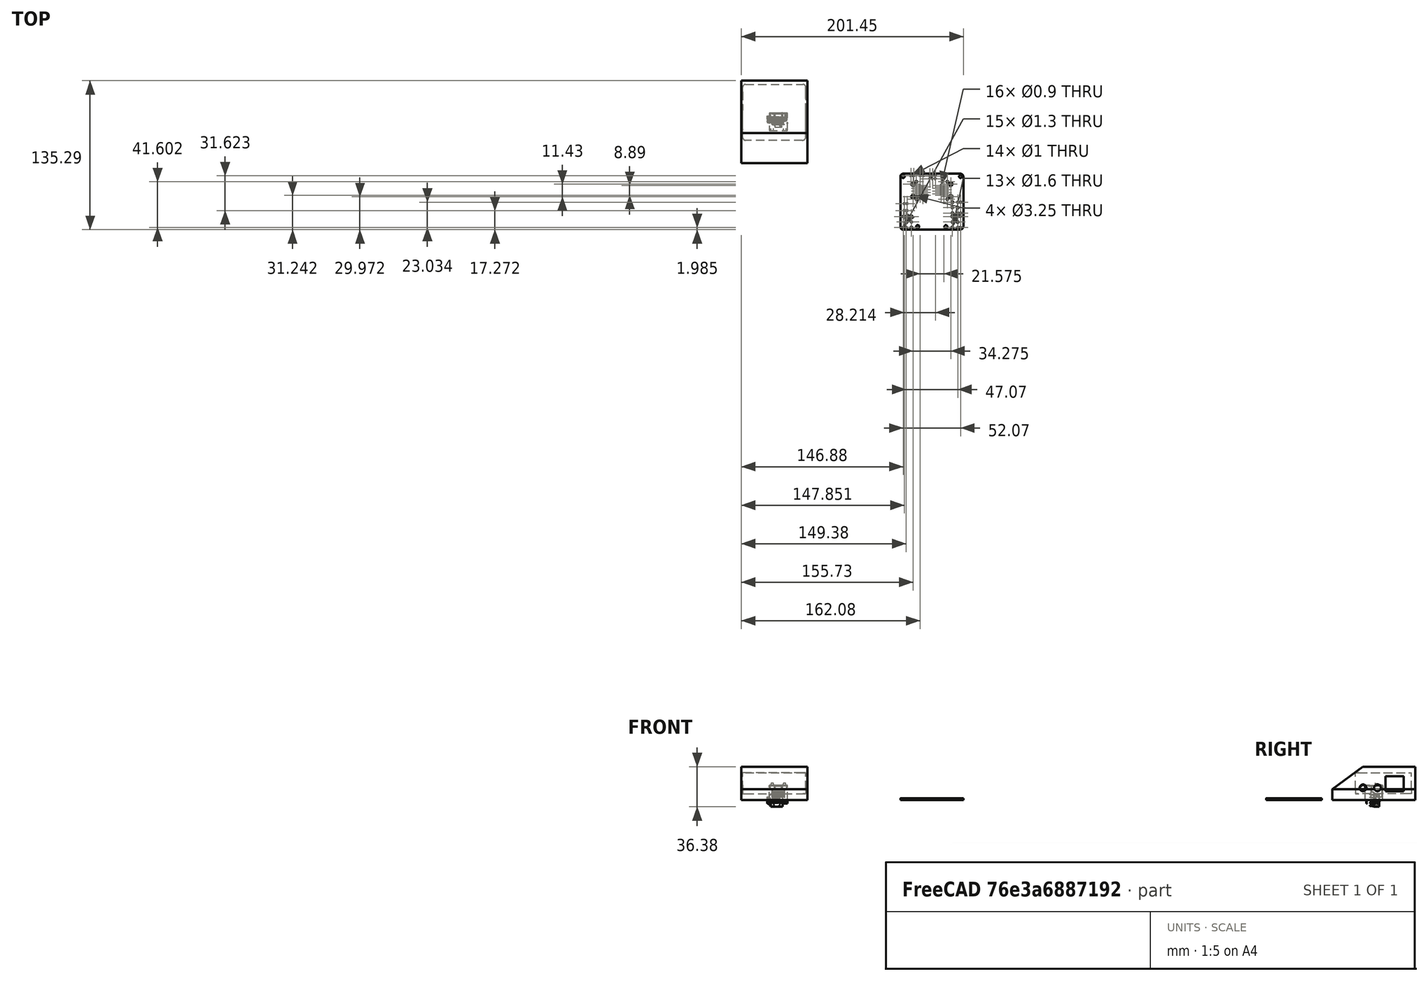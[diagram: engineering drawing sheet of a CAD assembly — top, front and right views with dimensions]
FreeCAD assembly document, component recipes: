
FREECAD ASSEMBLY — COMPONENT RECIPES ("Mikadapter81X")

This assembly document has 4 components, labeled P0..P3 below (a component is one placed body or linked part). 2 of them carry a construction recipe — the FreeCAD feature program that regenerates the part from scratch, quoted from this document or its linked companion documents; the rest are supplied as boundary geometry only. No exploded tour is included for this assembly.
COMPONENT P0 — recipe-attached ("Body", modeled in this document).
Construction recipe (the document's own serialized feature program — sketch geometry with constraints, then the solid features built on it; lengths are millimeters unless a unit is written):

FEATURE [PartDesign::SubShapeBinder] Binder
  BindMode = 0
  ClaimChildren = false
  Context = -> Body [Binder.]
  Fuse = false
  MakeFace = true
  PartialLoad = false
  Relative = true
  Support = -> [LinkGroup]
  _Version = 2
FEATURE [Sketcher::SketchObject] Sketch
  ExternalGeometry = -> [Binder]
  FullyConstrained = true
  MapMode = 5
  Support = -> [XY_Plane]
  sketch-geometry (4):
    g0: LineSegment StartX=-30 StartY=37.5 StartZ=0 EndX=30 EndY=37.5 EndZ=0
    g1: LineSegment StartX=30 StartY=37.5 StartZ=0 EndX=30 EndY=-37.5 EndZ=0
    g2: LineSegment StartX=30 StartY=-37.5 StartZ=0 EndX=-30 EndY=-37.5 EndZ=0
    g3: LineSegment StartX=-30 StartY=-37.5 StartZ=0 EndX=-30 EndY=37.5 EndZ=0
  constraints (11):
    c: Coincident(g0,g1)
    c: Coincident(g1,g2)
    c: Coincident(g2,g3)
    c: Coincident(g3,g0)
    c: Horizontal(g0)
    c: Horizontal(g2)
    c: Vertical(g1)
    c: Vertical(g3)
    c: Symmetric(g1,g0,g-1)
    c: Distance(g0) = 60
    c: Distance(g3) = 75
FEATURE [PartDesign::Pad] Pad
  Direction = (1,1,1)
  Length = 10
  Length2 = 100
  Profile = -> Sketch
  Type = 0
FEATURE [Sketcher::SketchObject] Sketch001
  ExternalGeometry = -> [Binder]
  FullyConstrained = true
  MapMode = 5
  Placement = pos=(0,0,10) rot=(0,0,1;0rad)
  Support = -> [Pad]
  sketch-geometry (8):
    g0: LineSegment StartX=-26.16 StartY=34.1318 StartZ=0 EndX=25.91 EndY=34.1318 EndZ=0
    g1: LineSegment StartX=-28.7 StartY=31.5918 StartZ=0 EndX=-28.7 EndY=-14.1282 EndZ=0
    g2: LineSegment StartX=-26.16 StartY=-16.6682 StartZ=0 EndX=25.275 EndY=-16.6682 EndZ=0
    g3: LineSegment StartX=28.45 StartY=31.5918 StartZ=0 EndX=28.45 EndY=-13.4932 EndZ=0
    g4: ArcOfCircle CenterX=-26.16 CenterY=31.5918 CenterZ=0 NormalX=0 NormalY=0 NormalZ=1 AngleXU=0 Radius=2.53997 StartAngle=1.57078 EndAngle=3.1416
    g5: ArcOfCircle CenterX=25.91 CenterY=31.5918 CenterZ=0 NormalX=0 NormalY=0 NormalZ=1 AngleXU=0 Radius=2.53999 StartAngle=6.28318 EndAngle=7.85399
    g6: ArcOfCircle CenterX=25.275 CenterY=-13.4932 CenterZ=0 NormalX=0 NormalY=0 NormalZ=1 AngleXU=0 Radius=3.17501 StartAngle=4.71239 EndAngle=6.28318
    g7: ArcOfCircle CenterX=-26.16 CenterY=-14.1282 CenterZ=0 NormalX=0 NormalY=0 NormalZ=1 AngleXU=0 Radius=2.53999 StartAngle=3.14159 EndAngle=4.71239
  constraints (20):
    c: Coincident(g0,g-3)
    c: Coincident(g0,g-3)
    c: Coincident(g1,g-5)
    c: Coincident(g-5,g1)
    c: Coincident(g2,g-7)
    c: Coincident(g2,g-7)
    c: Coincident(g3,g-9)
    c: Coincident(g3,g-9)
    c: Coincident(g4,g-4)
    c: Coincident(g4,g1)
    c: Coincident(g4,g0)
    c: Coincident(g5,g-10)
    c: Coincident(g5,g0)
    c: Coincident(g5,g3)
    c: Coincident(g6,g-8)
    c: Coincident(g6,g2)
    c: Coincident(g6,g3)
    c: Coincident(g7,g-6)
    c: Coincident(g7,g1)
    c: Coincident(g7,g2)
FEATURE [PartDesign::Pocket] Pocket
  BaseFeature = -> Pad
  Length = 4
  Length2 = 100
  Profile = -> Sketch001
  Type = 0
FEATURE [Sketcher::SketchObject] Sketch002
  ExternalGeometry = -> [Binder,Pocket]
  FullyConstrained = false
  MapMode = 5
  Placement = pos=(30,0,0) rot=(0.57735,0.57735,0.57735;2.0944rad)
  Support = -> [Pocket]
  sketch-geometry (6):
    g0: LineSegment StartX=10.6588 StartY=21.6555 StartZ=0 EndX=27.1688 EndY=21.6555 EndZ=0
    g1: LineSegment StartX=27.1688 StartY=21.6555 StartZ=0 EndX=27.1688 EndY=8.19554 EndZ=0
    g2: LineSegment StartX=27.1688 StartY=8.19554 StartZ=0 EndX=10.6588 EndY=8.19554 EndZ=0
    g3: LineSegment StartX=10.6588 StartY=8.19554 StartZ=0 EndX=10.6588 EndY=21.6555 EndZ=0
    g4: Circle CenterX=3.3622 CenterY=11.2293 CenterZ=0 NormalX=0 NormalY=0 NormalZ=1 AngleXU=0 Radius=3.00378
    g5: Circle CenterX=-9.8878 CenterY=11.2293 CenterZ=0 NormalX=0 NormalY=0 NormalZ=1 AngleXU=0 Radius=3.00378
  constraints (13):
    c: Coincident(g0,g1)
    c: Coincident(g1,g2)
    c: Coincident(g2,g3)
    c: Coincident(g3,g0)
    c: Horizontal(g0)
    c: Horizontal(g2)
    c: Vertical(g1)
    c: Vertical(g3)
    c: Coincident(g0,g-9)
    c: Coincident(g1,g-11)
    c: DistanceY(g4,g5) = 0
    c: DistanceX(g5,g4) = 13.25
    c: Equal(g4,g5)
FEATURE [PartDesign::Pocket] Pocket001
  BaseFeature = -> Pocket
  Length = 5
  Length2 = 100
  Profile = -> Sketch002
  Type = 0
FEATURE [PartDesign::SubShapeBinder] Binder001
  BindMode = 0
  ClaimChildren = false
  Context = -> Body [Binder001.]
  Fuse = false
  MakeFace = true
  PartialLoad = false
  Relative = true
  Support = -> [Binder]
  _Version = 2
FEATURE [PartDesign::Body] Body
  Group = -> [Sketch,Pad,Binder,Sketch001,Pocket,Sketch002,Pocket001,Binder001]
  Origin = -> Origin
  Tip = -> Pocket001
COMPONENT P1 — recipe-attached ("Body001", modeled in this document).
Construction recipe (the document's own serialized feature program — sketch geometry with constraints, then the solid features built on it; lengths are millimeters unless a unit is written):

FEATURE [PartDesign::SubShapeBinder] Binder003
  BindMode = 0
  ClaimChildren = false
  Fuse = false
  MakeFace = true
  PartialLoad = false
  Relative = true
  Support = -> [Body[Pocket001.]]
  _Version = 2
FEATURE [Sketcher::SketchObject] Sketch008
  ExternalGeometry = -> [Binder003]
  FullyConstrained = false
  MapMode = 5
  Placement = pos=(0,0,0) rot=(0.57735,0.57735,0.57735;2.0944rad)
  Support = -> [YZ_Plane001]
  sketch-geometry (4):
    g0: LineSegment StartX=-37.5 StartY=10 StartZ=0 EndX=37.5 EndY=10 EndZ=0
    g1: LineSegment StartX=37.5 StartY=10 StartZ=0 EndX=37.5 EndY=30.3769 EndZ=0
    g2: LineSegment StartX=-37.5 StartY=10 StartZ=0 EndX=-10.046 EndY=30.3769 EndZ=0
    g3: LineSegment StartX=-10.046 StartY=30.3769 StartZ=0 EndX=37.5 EndY=30.3769 EndZ=0
  constraints (7):
    c: Coincident(g0,g-3)
    c: Vertical(g1)
    c: Coincident(g2,g0)
    c: Coincident(g3,g2)
    c: Coincident(g3,g1)
    c: Horizontal(g3)
    c: Coincident(g1,g0)
FEATURE [PartDesign::Pad] Pad001
  Direction = (1,1,1)
  Length = 60
  Length2 = 100
  Midplane = true
  Placement = pos=(0,0,0) rot=(0.57735,0.57735,0.57735;2.0944rad)
  Profile = -> Sketch008
  Type = 0
FEATURE [PartDesign::SubShapeBinder] Binder004
  BindMode = 0
  ClaimChildren = false
  Context = -> Body001 [Binder004.]
  Fuse = false
  MakeFace = true
  PartialLoad = false
  Relative = true
  Support = -> [LinkGroup]
  _Version = 2
FEATURE [Sketcher::SketchObject] Sketch009
  ExternalGeometry = -> [Binder004]
  FullyConstrained = false
  MapMode = 5
  Placement = pos=(-2.8e-15,1.6e-15,10) rot=(0.707107,0.707107,0;3.14159rad)
  Support = -> [Pad001]
  sketch-geometry (8):
    g0: LineSegment StartX=-16.6682 StartY=25.275 StartZ=0 EndX=-16.6682 EndY=-26.16 EndZ=0
    g1: LineSegment StartX=-14.1282 StartY=-28.7 StartZ=0 EndX=31.5918 EndY=-28.7 EndZ=0
    g2: LineSegment StartX=34.1318 StartY=-26.16 StartZ=0 EndX=34.1318 EndY=25.91 EndZ=0
    g3: ArcOfCircle CenterX=-13.4932 CenterY=25.275 CenterZ=0 NormalX=0 NormalY=0 NormalZ=1 AngleXU=0 Radius=3.17501 StartAngle=1.5708 EndAngle=3.14159
    g4: ArcOfCircle CenterX=31.5918 CenterY=25.91 CenterZ=0 NormalX=0 NormalY=0 NormalZ=1 AngleXU=0 Radius=2.53999 StartAngle=6.28318 EndAngle=7.85399
    g5: ArcOfCircle CenterX=-14.1282 CenterY=-26.16 CenterZ=0 NormalX=0 NormalY=0 NormalZ=1 AngleXU=0 Radius=2.53999 StartAngle=3.14159 EndAngle=4.71239
    g6: ArcOfCircle CenterX=31.5918 CenterY=-26.16 CenterZ=0 NormalX=0 NormalY=0 NormalZ=1 AngleXU=0 Radius=2.53997 StartAngle=4.71238 EndAngle=6.28319
    g7: LineSegment StartX=-13.4932 StartY=28.45 StartZ=0 EndX=31.5918 EndY=28.45 EndZ=0
  constraints (15):
    c: Coincident(g1,g-4)
    c: Coincident(g1,g-4)
    c: Coincident(g3,g-9)
    c: Coincident(g3,g0)
    c: Coincident(g4,g-8)
    c: Coincident(g4,g2)
    c: Coincident(g4,g-10)
    c: Coincident(g5,g-6)
    c: Coincident(g5,g0)
    c: Coincident(g5,g1)
    c: Coincident(g6,g-5)
    c: Coincident(g6,g1)
    c: Coincident(g6,g2)
    c: Coincident(g7,g3)
    c: Coincident(g7,g4)
FEATURE [PartDesign::Pocket] Pocket002
  BaseFeature = -> Pad001
  Length = 15
  Length2 = 100
  Placement = pos=(0,0,0) rot=(0.57735,0.57735,0.57735;2.0944rad)
  Profile = -> Sketch009
  Type = 0
FEATURE [Sketcher::SketchObject] Sketch010
  ExternalGeometry = -> [Binder004]
  FullyConstrained = false
  MapMode = 5
  Placement = pos=(-30,2e-14,-1e-14) rot=(-0.57735,-0.57735,0.57735;2.0944rad)
  Support = -> [Pocket002]
  sketch-geometry (5):
    g0: LineSegment StartX=10.6588 StartY=-8.19554 StartZ=0 EndX=27.3788 EndY=-8.19554 EndZ=0
    g1: LineSegment StartX=27.3788 StartY=-8.19554 StartZ=0 EndX=27.3788 EndY=-21.6555 EndZ=0
    g2: LineSegment StartX=27.3788 StartY=-21.6555 StartZ=0 EndX=10.6588 EndY=-21.6555 EndZ=0
    g3: LineSegment StartX=10.6588 StartY=-21.6555 StartZ=0 EndX=10.6588 EndY=-8.19554 EndZ=0
    g4: Circle CenterX=-9.63407 CenterY=-10.7296 CenterZ=0 NormalX=0 NormalY=0 NormalZ=1 AngleXU=0 Radius=2.95108
  constraints (11):
    c: Coincident(g0,g1)
    c: Coincident(g1,g2)
    c: Coincident(g2,g3)
    c: Coincident(g3,g0)
    c: Horizontal(g0)
    c: Horizontal(g2)
    c: Vertical(g1)
    c: Vertical(g3)
    c: Coincident(g0,g-5)
    c: Coincident(g1,g-7)
    c: PointOnObject(g-4,g4)
FEATURE [PartDesign::Pocket] Pocket003
  BaseFeature = -> Pocket002
  Length = 5
  Length2 = 100
  Placement = pos=(0,0,0) rot=(0.57735,0.57735,0.57735;2.0944rad)
  Profile = -> Sketch010
  Type = 0
FEATURE [Sketcher::SketchObject] Sketch011
  ExternalGeometry = -> [Binder004]
  FullyConstrained = false
  MapMode = 5
  Placement = pos=(30,-2.66e-14,1.33e-14) rot=(0.57735,0.57735,0.57735;2.0944rad)
  Support = -> [Pocket003]
  sketch-geometry (6):
    g0: Circle CenterX=3.35639 CenterY=11.2599 CenterZ=0 NormalX=0 NormalY=0 NormalZ=1 AngleXU=0 Radius=3.06858
    g1: Circle CenterX=-9.69989 CenterY=11.2211 CenterZ=0 NormalX=0 NormalY=0 NormalZ=1 AngleXU=0 Radius=3.06858
    g2: LineSegment StartX=10.6588 StartY=21.6555 StartZ=0 EndX=27.1688 EndY=21.6555 EndZ=0
    g3: LineSegment StartX=27.1688 StartY=21.6555 StartZ=0 EndX=27.1688 EndY=8.19554 EndZ=0
    g4: LineSegment StartX=27.1688 StartY=8.19554 StartZ=0 EndX=10.6588 EndY=8.19554 EndZ=0
    g5: LineSegment StartX=10.6588 StartY=8.19554 StartZ=0 EndX=10.6588 EndY=21.6555 EndZ=0
  constraints (11):
    c: Equal(g0,g1)
    c: Coincident(g2,g3)
    c: Coincident(g3,g4)
    c: Coincident(g4,g5)
    c: Coincident(g5,g2)
    c: Horizontal(g2)
    c: Horizontal(g4)
    c: Vertical(g3)
    c: Vertical(g5)
    c: Coincident(g2,g-3)
    c: Coincident(g3,g-6)
FEATURE [PartDesign::Pocket] Pocket004
  BaseFeature = -> Pocket003
  Length = 5
  Length2 = 100
  Placement = pos=(0,0,0) rot=(0.57735,0.57735,0.57735;2.0944rad)
  Profile = -> Sketch011
  Type = 0
FEATURE [PartDesign::Body] Body001
  Group = -> [Sketch008,Binder003,Pad001,Sketch009,Binder004,Pocket002,Sketch010,Pocket003,Sketch011,Pocket004]
  Origin = -> Origin001
  Tip = -> Pocket004
COMPONENT P2 — geometry summary ("RJ45_Amphenol_RJHSE538X001"; no construction recipe available for this part):
  bounding box: 56.6 x 18.7 x 16.7 mm
  tessellated surface: 30,984 triangles
  volume: 4892 mm^3 (28% of its bounding box)
  symmetry: 2-fold rotationally symmetric about the z axis
COMPONENT P3 — geometry summary ("FC68132"; no construction recipe available for this part):
  bounding box: 60.1 x 25.0 x 10.0 mm
  tessellated surface: 18,504 triangles
  volume: 2223 mm^3 (15% of its bounding box)
PROVENANCE & LICENSES
A FreeCAD (.FCStd) document from a public repository crawl; recipes are the document's own serialized feature recipes (and, for linked parts, companion documents' recipes).
License: as declared in the source repository (recorded in the dataset sidecar).
